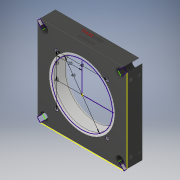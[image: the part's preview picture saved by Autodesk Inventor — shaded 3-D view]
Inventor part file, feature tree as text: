
AUTODESK INVENTOR PART (.ipt)
format: ipt  version: 2017 (Build 210142000, 142)  size: 900,608 bytes
history: native  units: mm
features: extrude x2, sketch x1, hole x1, fillet x1, other x1
ambient origin geometry x8: Origin, YZ Plane, XZ Plane, XY Plane, X Axis, Y Axis, Z Axis, Center Point
bodies: Solid1 (feature_tree)
feature tree (6):
  sketch  "Sketch4"  dims[d40=48.0mm d41=20.0mm d42=20.0mm d43=20.0mm d45=40.0mm d46=20.0mm d48=40.0mm d51=2.5mm d52=6.0mm d53=4.0mm d54=2.0mm d55=90.0deg d56=8.0mm d57=20.594885mm d58=10.0mm d59=0.0mm d60=2.0mm d61=10.0mm d62=0.0mm]
  hole  "Hole5"  [1 undecoded]
  extrude  "Extrusion3"  Depth=20.0mm
  fillet  "Fillet1"  Radius=20.0mm
  extrude  "Extrusion4"  Depth=10.0mm TaperAngle=0.0deg
  other  "13108-001-1-solid1"
note: 1 required parameter value undecoded (feature->parameter linkage not recoverable at this tier; creation-order binding heuristic only, values carry confidence <= 0.55)
